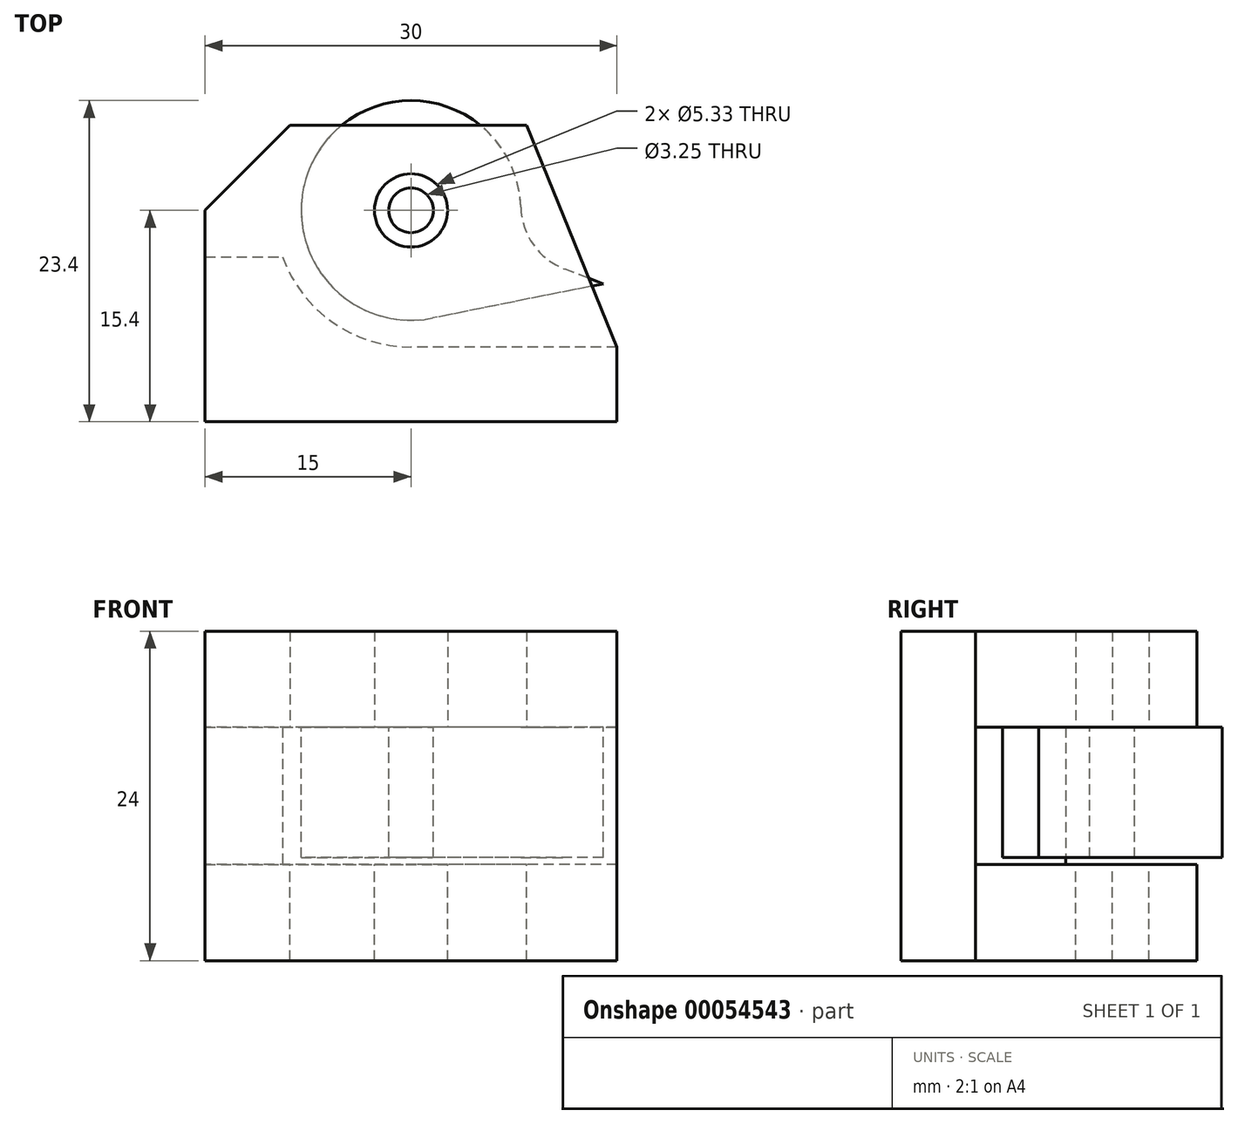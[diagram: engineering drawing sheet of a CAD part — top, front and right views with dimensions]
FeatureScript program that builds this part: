
annotation { "Feature Type Name" : "Feature", "Feature Type Description" : "" }
export const myFeature = defineFeature(function(context is Context, id is Id, definition is map)
    precondition{}
    {
        {
            var Q0;
            Q0=qCreatedBy(makeId("Top.planeOp"),FACE);
            var sketch = newSketch(context, id + "F0", { "sketchPlane" : qUnion([Q0])});
            skLineSegment(sketch, "E0", {"start": v(0, 0) * mm, "end": v(14.01, -5.35) * mm});
            skLineSegment(sketch, "E1", {"start": v(14.01, -5.35) * mm, "end": v(5.8, 68.2) * mm});
            skLineSegment(sketch, "E2", {"start": v(5.8, 68.2) * mm, "end": v(-10, 0) * mm});
            skText(sketch, "E3", { "text": "Move this point\n(counter-clockwise)", "fontName": "OpenSans-Regular.ttf"});
            skText(sketch, "E4", { "text": "To here ->", "fontName": "OpenSans-Regular.ttf"});
            const initialGuessF0  = {"E3": [0.01401, -0.00946, 1, 0, 0.0041], "E4": [-0.06827, 0.0051, 1, 0, 0.00496]};
            skSetInitialGuess(sketch, initialGuessF0);
            skSolve(sketch);
        }
        {
            var Q0;
            Q0=qCreatedBy(makeId("Top.planeOp"),FACE);
            var sketch = newSketch(context, id + "F1", { "sketchPlane" : qUnion([Q0])});
            skLineSegment(sketch, "E5", {"start": v(-15, 0) * mm, "end": v(-15, -15.4) * mm});
            skLineSegment(sketch, "E6", {"start": v(-15, -15.4) * mm, "end": v(15, -15.4) * mm});
            skLineSegment(sketch, "E7", {"start": v(15, -15.4) * mm, "end": v(15, -9.95) * mm});
            skLineSegment(sketch, "E8", {"start": v(8.43, 6.19) * mm, "end": v(-8.81, 6.19) * mm});
            skLineSegment(sketch, "E9", {"start": v(-8.81, 6.19) * mm, "end": v(-15, 0) * mm});
            skLineSegment(sketch, "E10", {"start": v(0, 0) * mm, "end": v(15, -9.95) * mm, "construction": true});
            skLineSegment(sketch, "E11", {"start": v(8.43, 6.19) * mm, "end": v(15, -9.95) * mm});
            skCircle(sketch, "E12", {"center": v(0, 0) * mm, "radius": 4.2 * mm});
            skCircle(sketch, "E13", {"center": v(0, 0) * mm, "radius": 2.67 * mm});
            skSolve(sketch);
        }
        {
            var Q0;
            Q0=qCreatedBy(makeId("Top.planeOp"),FACE);
            var sketch = newSketch(context, id + "F2", { "sketchPlane" : qUnion([Q0])});
            skLineSegment(sketch, "E14", {"start": v(14.01, -5.35) * mm, "end": v(11.21, -4.28) * mm});
            skLineSegment(sketch, "E15", {"start": v(14.01, -5.35) * mm, "end": v(1.57, -7.84) * mm});
            skArc(sketch, "E16", {"start": v(1.57, -7.84) * mm, "mid": v(-6.26, 4.98) * mm, "end": v(8, 0.24) * mm});
            skCircle(sketch, "E17", {"center": v(0, 0) * mm, "radius": 1.63 * mm});
            skPoint(sketch, "E18.visualSharp", {"position": v(7.47, -2.85) * mm});
            skArc(sketch, "E18.filletArc", {"start": v(8, 0.24) * mm, "mid": v(8.92, -2.5) * mm, "end": v(11.21, -4.28) * mm});
            skSolve(sketch);
        }
        {
            var Q0;
            Q0 = qSketchRegion(id + "F1", true);
            var Q1;
            Q1=makeQuery(id+"F1.imprint","IMPRINT",FACE,{"disambiguationData":[TD([[makeQuery(id+"F1.imprint","IMPRINT",EDGE,{"derivedFrom":sQuery(id+"F1.wireOp",EDGE,"E12")}),1.0]])]});
            extrude(context, id + "F3", {"entities" : qUnion([Q0, Q1]), "depth" : 7 * mm});
        }
        {
            var Q0;
            Q0=makeQuery(id+"F3.opExtrude","CAP_FACE",FACE,{"disambiguationData":[OSD([sQuery(id+"F1.wireOp",EDGE,"E5"),sQuery(id+"F1.wireOp",EDGE,"E6"),sQuery(id+"F1.wireOp",EDGE,"E7"),sQuery(id+"F1.wireOp",EDGE,"E8"),sQuery(id+"F1.wireOp",EDGE,"E9"),sQuery(id+"F1.wireOp",EDGE,"E11"),sQuery(id+"F1.wireOp",EDGE,"E13")])],"isStart":true});
            cPlane(context, id + "F4", {"entities" : qUnion([Q0]), "cplaneType" : CPlaneType.OFFSET, "offset" : 10 * mm, "width" : 150 * mm, "height" : 150 * mm});
        }
        {
            var Q0;
            Q0=qCreatedBy(id+"F4.planeOp",FACE);
            var sketch = newSketch(context, id + "F5", { "sketchPlane" : qUnion([Q0])});
            skLineSegment(sketch, "E19.1.0", {"start": v(-8.81, -6.19) * mm, "end": v(-15, 0) * mm});
            skLineSegment(sketch, "E19.1.1", {"start": v(-15, 0) * mm, "end": v(-15, 15.4) * mm});
            skLineSegment(sketch, "E19.1.2", {"start": v(-15, 15.4) * mm, "end": v(15, 15.4) * mm});
            skLineSegment(sketch, "E19.1.3", {"start": v(15, 15.4) * mm, "end": v(15, 9.95) * mm});
            skLineSegment(sketch, "E19.1.4", {"start": v(15, 9.95) * mm, "end": v(8.43, -6.19) * mm});
            skLineSegment(sketch, "E19.1.5", {"start": v(8.43, -6.19) * mm, "end": v(-8.81, -6.19) * mm});
            skCircle(sketch, "E20.0", {"center": v(0, 0) * mm, "radius": 2.67 * mm});
            skSolve(sketch);
        }
        {
            var Q0;
            Q0=makeQuery(id+"F5.imprint","IMPRINT",FACE,{"disambiguationData":[TD([[makeQuery(id+"F5.imprint","IMPRINT",EDGE,{"derivedFrom":sQuery(id+"F5.wireOp",EDGE,"E19.1.0")}),-1.0]])]});
            extrude(context, id + "F6", {"entities" : qUnion([Q0]), "depth" : 7 * mm});
        }
        {
            var Q0;
            Q0 = qSketchRegion(id + "F2", true);
            extrude(context, id + "F7", {"entities" : qUnion([Q0]), "oppositeDirection" : true, "depth" : 9.5 * mm});
        }
        {
            var Q0;
            Q0=sQuery(id+"F0.wireOp",EDGE,"E1");
            var Q1;
            Q1=sQuery(id+"F0.wireOp",EDGE,"E2");
            var Q2;
            Q2=makeQuery(id+"F3.opExtrude","CAP_FACE",FACE,{"disambiguationData":[OSD([sQuery(id+"F1.wireOp",EDGE,"E5"),sQuery(id+"F1.wireOp",EDGE,"E6"),sQuery(id+"F1.wireOp",EDGE,"E7"),sQuery(id+"F1.wireOp",EDGE,"E8"),sQuery(id+"F1.wireOp",EDGE,"E9"),sQuery(id+"F1.wireOp",EDGE,"E11"),sQuery(id+"F1.wireOp",EDGE,"E13")])],"isStart":false});
            var Q3;
            Q3=makeQuery(id+"F6.opExtrude","CAP_FACE",FACE,{"disambiguationData":[OSD([sQuery(id+"F5.wireOp",EDGE,"E19.1.0"),sQuery(id+"F5.wireOp",EDGE,"E19.1.1"),sQuery(id+"F5.wireOp",EDGE,"E19.1.2"),sQuery(id+"F5.wireOp",EDGE,"E19.1.3"),sQuery(id+"F5.wireOp",EDGE,"E19.1.4"),sQuery(id+"F5.wireOp",EDGE,"E19.1.5"),sQuery(id+"F5.wireOp",EDGE,"E20.0")])],"isStart":false});
            extrude(context, id + "F8", {"bodyType" : ToolBodyType.SURFACE, "surfaceEntities" : qUnion([Q0, Q1]), "endBound" : BoundingType.UP_TO_SURFACE, "endBoundEntityFace" : qUnion([Q2]), "depth" : 25 * mm, "hasSecondDirection" : true, "secondDirectionBound" : SecondDirectionBoundingType.UP_TO_SURFACE, "secondDirectionOppositeDirection" : true, "secondDirectionBoundEntityFace" : qUnion([Q3]), "secondDirectionDepth" : 25 * mm});
        }
        {
            var Q0;
            Q0=makeQuery(id+"F6.opExtrude","CAP_FACE",FACE,{"disambiguationData":[OSD([sQuery(id+"F5.wireOp",EDGE,"E19.1.0"),sQuery(id+"F5.wireOp",EDGE,"E19.1.1"),sQuery(id+"F5.wireOp",EDGE,"E19.1.2"),sQuery(id+"F5.wireOp",EDGE,"E19.1.3"),sQuery(id+"F5.wireOp",EDGE,"E19.1.4"),sQuery(id+"F5.wireOp",EDGE,"E19.1.5"),sQuery(id+"F5.wireOp",EDGE,"E20.0")])],"isStart":true});
            var sketch = newSketch(context, id + "F9", { "sketchPlane" : qUnion([Q0])});
            skLineSegment(sketch, "E21", {"start": v(-15, -3.4) * mm, "end": v(-9.35, -3.4) * mm});
            skLineSegment(sketch, "E22", {"start": v(15, -9.95) * mm, "end": v(0, -9.95) * mm});
            skArc(sketch, "E23", {"start": v(-9.35, -3.4) * mm, "mid": v(-5.7, -8.15) * mm, "end": v(0, -9.95) * mm});
            skLineSegment(sketch, "E24", {"start": v(15, -9.95) * mm, "end": v(15, -15.4) * mm});
            skLineSegment(sketch, "E25", {"start": v(15, -15.4) * mm, "end": v(-15, -15.4) * mm});
            skLineSegment(sketch, "E26", {"start": v(-15, -15.4) * mm, "end": v(-15, -3.4) * mm});
            skSolve(sketch);
        }
        {
            var Q0;
            Q0 = qSketchRegion(id + "F9", true);
            var Q1;
            Q1=makeQuery(id+"F3.opExtrude","CAP_FACE",FACE,{"disambiguationData":[OSD([sQuery(id+"F1.wireOp",EDGE,"E5"),sQuery(id+"F1.wireOp",EDGE,"E6"),sQuery(id+"F1.wireOp",EDGE,"E7"),sQuery(id+"F1.wireOp",EDGE,"E8"),sQuery(id+"F1.wireOp",EDGE,"E9"),sQuery(id+"F1.wireOp",EDGE,"E11"),sQuery(id+"F1.wireOp",EDGE,"E13")])],"isStart":true});
            extrude(context, id + "F10", {"entities" : qUnion([Q0]), "operationType" : NewBodyOperationType.ADD, "endBound" : BoundingType.UP_TO_SURFACE, "endBoundEntityFace" : qUnion([Q1]), "depth" : 25 * mm});
        }
    });
